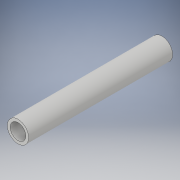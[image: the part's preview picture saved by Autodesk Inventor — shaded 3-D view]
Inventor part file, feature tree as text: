
AUTODESK INVENTOR PART (.ipt)
format: ipt  version: 2019 (Build 230136000, 136)  size: 98,816 bytes
history: native  units: mm
features: extrude x2, sketch x2
ambient origin geometry x8: Origin, YZ Plane, XZ Plane, XY Plane, X Axis, Y Axis, Z Axis, Center Point
bodies: Solid1 (feature_tree)
feature tree (4):
  extrude  "Extrusion1"  Depth=1012.64mm TaperAngle=0.0deg
  extrude  "Extrusion2"  Depth=101.264mm TaperAngle=0.0deg
  sketch  "Sketch1"  dims[d0=150.0mm d1=1012.64mm d2=0.0mm]
  sketch  "Sketch2"  dims[d3=110.0mm d4=101.264mm d5=0.0mm]
